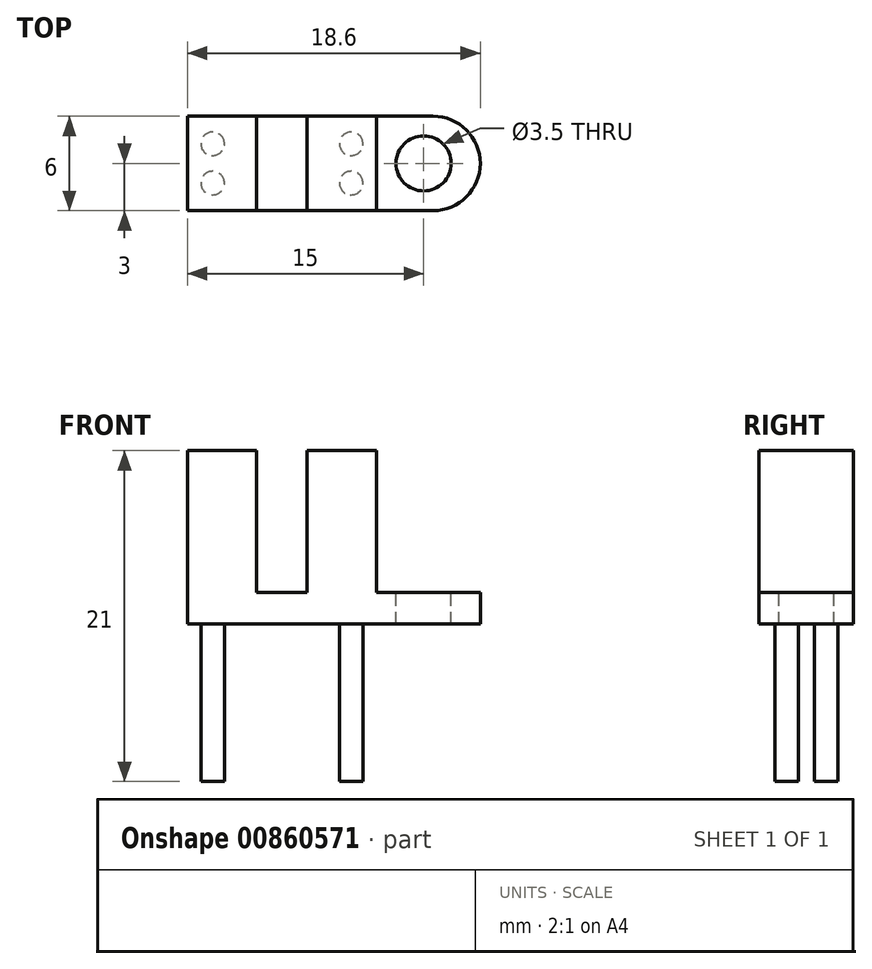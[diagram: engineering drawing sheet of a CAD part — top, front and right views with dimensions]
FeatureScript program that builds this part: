
annotation { "Feature Type Name" : "Feature", "Feature Type Description" : "" }
export const myFeature = defineFeature(function(context is Context, id is Id, definition is map)
    precondition{}
    {
        {
            var Q0;
            Q0=qCreatedBy(makeId("Top.planeOp"),FACE);
            var sketch = newSketch(context, id + "F0", { "sketchPlane" : qUnion([Q0])});
            skLineSegment(sketch, "E0.bottom", {"start": v(-6, 3) * mm, "end": v(6, 3) * mm});
            skLineSegment(sketch, "E0.top", {"start": v(-6, -3) * mm, "end": v(6, -3) * mm});
            skLineSegment(sketch, "E0.left", {"start": v(-6, 3) * mm, "end": v(-6, -3) * mm});
            skLineSegment(sketch, "E0.right", {"start": v(6, 3) * mm, "end": v(6, -3) * mm, "construction": true});
            skLineSegment(sketch, "E1", {"start": v(-6, 3) * mm, "end": v(6, -3) * mm, "construction": true});
            skLineSegment(sketch, "E2", {"start": v(6, 3) * mm, "end": v(9.6, 3) * mm});
            skLineSegment(sketch, "E3", {"start": v(6, -3) * mm, "end": v(9.6, -3) * mm});
            skLineSegment(sketch, "E4", {"start": v(9.6, -3) * mm, "end": v(9.6, 3) * mm, "construction": true});
            skArc(sketch, "E5", {"start": v(9.6, 3) * mm, "mid": v(12.6, 0) * mm, "end": v(9.6, -3) * mm});
            skSolve(sketch);
        }
        {
            var Q0;
            Q0 = qSketchRegion(id + "F0", true);
            extrude(context, id + "F1", {"entities" : qUnion([Q0]), "depth" : 2 * mm, "offsetDistance" : 25 * mm});
        }
        {
            var Q0;
            Q0=makeQuery(id+"F1.opExtrude","CAP_FACE",FACE,{"disambiguationData":[OSD([sQuery(id+"F0.wireOp",EDGE,"E0.bottom"),sQuery(id+"F0.wireOp",EDGE,"E0.top"),sQuery(id+"F0.wireOp",EDGE,"E0.left"),sQuery(id+"F0.wireOp",EDGE,"E2"),sQuery(id+"F0.wireOp",EDGE,"E3"),sQuery(id+"F0.wireOp",EDGE,"E5")])],"isStart":false});
            var sketch = newSketch(context, id + "F2", { "sketchPlane" : qUnion([Q0])});
            skLineSegment(sketch, "E6.bottom", {"start": v(-6, -3) * mm, "end": v(-1.6, -3) * mm});
            skLineSegment(sketch, "E6.top", {"start": v(-6, 3) * mm, "end": v(-1.6, 3) * mm});
            skLineSegment(sketch, "E6.left", {"start": v(-6, -3) * mm, "end": v(-6, 3) * mm});
            skLineSegment(sketch, "E6.right", {"start": v(-1.6, -3) * mm, "end": v(-1.6, 3) * mm});
            skLineSegment(sketch, "E7.bottom", {"start": v(1.6, -3) * mm, "end": v(6, -3) * mm});
            skLineSegment(sketch, "E7.top", {"start": v(1.6, 3) * mm, "end": v(6, 3) * mm});
            skLineSegment(sketch, "E7.left", {"start": v(1.6, -3) * mm, "end": v(1.6, 3) * mm});
            skLineSegment(sketch, "E7.right", {"start": v(6, -3) * mm, "end": v(6, 3) * mm});
            skLineSegment(sketch, "E8", {"start": v(-6, 3) * mm, "end": v(6, -3) * mm, "construction": true});
            skSolve(sketch);
        }
        {
            var Q0;
            Q0 = qSketchRegion(id + "F2", true);
            extrude(context, id + "F3", {"entities" : qUnion([Q0]), "operationType" : NewBodyOperationType.ADD, "depth" : 9 * mm, "offsetDistance" : 25 * mm});
        }
        {
            var Q0;
            Q0=makeQuery(id+"F1.opExtrude","CAP_FACE",FACE,{"disambiguationData":[OSD([sQuery(id+"F0.wireOp",EDGE,"E0.bottom"),sQuery(id+"F0.wireOp",EDGE,"E0.top"),sQuery(id+"F0.wireOp",EDGE,"E0.left"),sQuery(id+"F0.wireOp",EDGE,"E2"),sQuery(id+"F0.wireOp",EDGE,"E3"),sQuery(id+"F0.wireOp",EDGE,"E5")])],"isStart":true});
            var sketch = newSketch(context, id + "F4", { "sketchPlane" : qUnion([Q0])});
            skLineSegment(sketch, "E9.bottom", {"start": v(-4.4, 1.25) * mm, "end": v(4.4, 1.25) * mm, "construction": true});
            skLineSegment(sketch, "E9.top", {"start": v(-4.4, -1.25) * mm, "end": v(4.4, -1.25) * mm, "construction": true});
            skLineSegment(sketch, "E9.left", {"start": v(-4.4, 1.25) * mm, "end": v(-4.4, -1.25) * mm, "construction": true});
            skLineSegment(sketch, "E9.right", {"start": v(4.4, 1.25) * mm, "end": v(4.4, -1.25) * mm, "construction": true});
            skLineSegment(sketch, "E10", {"start": v(-4.4, 1.25) * mm, "end": v(4.4, -1.25) * mm, "construction": true});
            skCircle(sketch, "E11", {"center": v(-4.4, 1.25) * mm, "radius": 0.75 * mm});
            skCircle(sketch, "E12", {"center": v(4.4, 1.25) * mm, "radius": 0.75 * mm});
            skCircle(sketch, "E13", {"center": v(4.4, -1.25) * mm, "radius": 0.75 * mm});
            skCircle(sketch, "E14", {"center": v(-4.4, -1.25) * mm, "radius": 0.75 * mm});
            skSolve(sketch);
        }
        {
            var Q0;
            Q0 = qSketchRegion(id + "F4", true);
            extrude(context, id + "F5", {"entities" : qUnion([Q0]), "operationType" : NewBodyOperationType.ADD, "depth" : 10 * mm, "offsetDistance" : 25 * mm});
        }
        {
            var Q0;
            {var subQ0=sQuery(id+"F0.wireOp",EDGE,"E5");var subQ1=sQuery(id+"F0.wireOp",EDGE,"E3");var subQ2=sQuery(id+"F0.wireOp",EDGE,"E0.top");var subQ3=sQuery(id+"F0.wireOp",EDGE,"E2");var subQ4=sQuery(id+"F0.wireOp",EDGE,"E0.bottom");Q0=makeQuery(id+"F3.boolean.opBoolean","SPLIT",FACE,{"disambiguationData":[TD([makeQuery(id+"F1.opExtrude","SWEPT_FACE",FACE,{"disambiguationData":[OSD([subQ0])]})])],"derivedFrom":makeQuery(id+"F1.opExtrude","CAP_FACE",FACE,{"disambiguationData":[OSD([subQ4,subQ2,sQuery(id+"F0.wireOp",EDGE,"E0.left"),subQ3,subQ1,subQ0])],"isStart":false})});}
            var sketch = newSketch(context, id + "F6", { "sketchPlane" : qUnion([Q0])});
            skCircle(sketch, "E15", {"center": v(9, 0) * mm, "radius": 1.75 * mm});
            skLineSegment(sketch, "E16", {"start": v(0, 0) * mm, "end": v(9, 0) * mm, "construction": true});
            skSolve(sketch);
        }
        {
            var Q0;
            Q0 = qSketchRegion(id + "F6", true);
            extrude(context, id + "F7", {"entities" : qUnion([Q0]), "operationType" : NewBodyOperationType.REMOVE, "endBound" : BoundingType.THROUGH_ALL, "oppositeDirection" : true, "depth" : 25 * mm, "offsetDistance" : 25 * mm});
        }
    });
